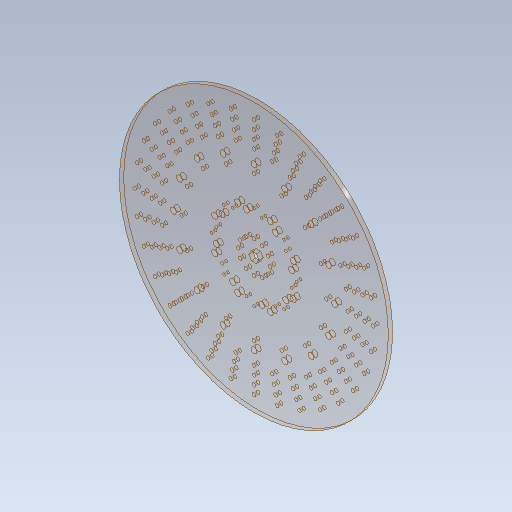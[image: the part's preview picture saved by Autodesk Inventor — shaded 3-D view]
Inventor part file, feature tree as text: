
AUTODESK INVENTOR PART (.ipt)
format: ipt  version: 2020 (Build 240168000, 168)  size: 452,608 bytes
history: native  units: in
note: dims shown in document units (in); Inventor stores cm internally (conversion verified against a paired STEP export)
features: other x3, sketch x2
ambient origin geometry x8: Origin, YZ Plane, XZ Plane, XY Plane, X Axis, Y Axis, Z Axis, Center Point
bodies: Solid1 (feature_tree)
feature tree (5):
  other  "IndexWheelFlatPlatesPolyOutside.ipt"
  other  "Solid1::IndexWheelFlatPlatesPolyOutside.ipt"
  other  "TaggingFeature1"
  sketch  "Sketch1"  dims[d0=0.3937in]
  sketch  "Sketch2"
